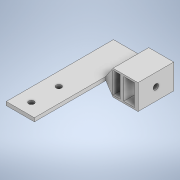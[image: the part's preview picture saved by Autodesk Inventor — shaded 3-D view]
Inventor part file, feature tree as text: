
AUTODESK INVENTOR PART (.ipt)
format: ipt  version: 2020 (Build 240168000, 168)  size: 189,440 bytes
history: native  units: in
note: dims shown in document units (in); Inventor stores cm internally (conversion verified against a paired STEP export)
features: extrude x6, sketch x6
ambient origin geometry x8: Origin, YZ Plane, XZ Plane, XY Plane, X Axis, Y Axis, Z Axis, Center Point
bodies: Solid1 (feature_tree)
feature tree (12):
  extrude  "Extrusion1"  Depth=1.0in
  extrude  "Extrusion2"  Depth=0.2in TaperAngle=0.0deg
  extrude  "Extrusion3"  Depth=0.1in
  extrude  "Extrusion5"  Depth=0.6in
  extrude  "Extrusion7"  Depth=0.6in
  extrude  "Extrusion9"  Depth=2.0in TaperAngle=0.0deg
  sketch  "Sketch1"  dims[d0=0.7874in d1=1.0in]
  sketch  "Sketch2"  dims[d2=0.1in d3=0.0in d4=0.2in d5=0.0in]
  sketch  "Sketch4"  dims[d6=0.3in d7=0.1in]
  sketch  "Sketch6"  dims[d9=0.3in d10=0.6in]
  sketch  "Sketch8"  dims[d11=1.0in d12=0.0in d16=0.6in]
  sketch  "Sketch10"  dims[d17=0.15in d18=0.5625in d19=0.0in d24=2.0in d25=0.0in d30=0.7in d31=0.77in d32=0.15in d33=0.15in d34=2.0in d35=0.0in]
